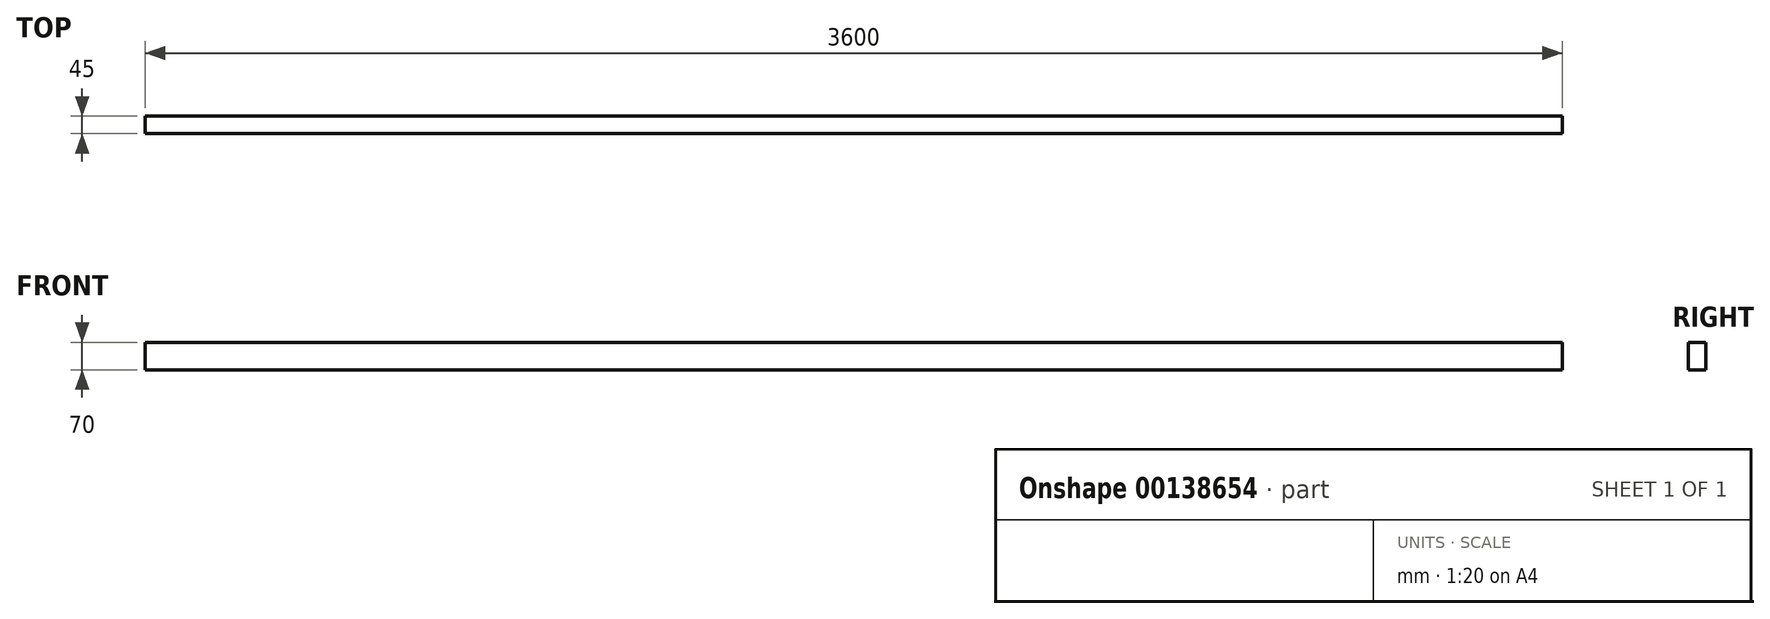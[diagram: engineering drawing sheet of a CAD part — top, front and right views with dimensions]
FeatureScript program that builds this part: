
annotation { "Feature Type Name" : "Feature", "Feature Type Description" : "" }
export const myFeature = defineFeature(function(context is Context, id is Id, definition is map)
    precondition{}
    {
        {
            var Q0;
            Q0=qCreatedBy(makeId("Right.planeOp"),FACE);
            var sketch = newSketch(context, id + "F0", { "sketchPlane" : qUnion([Q0])});
            skLineSegment(sketch, "E0.bottom", {"start": v(22.5, 35) * mm, "end": v(-22.5, 35) * mm});
            skLineSegment(sketch, "E0.top", {"start": v(22.5, -35) * mm, "end": v(-22.5, -35) * mm});
            skLineSegment(sketch, "E0.left", {"start": v(22.5, 35) * mm, "end": v(22.5, -35) * mm});
            skLineSegment(sketch, "E0.right", {"start": v(-22.5, 35) * mm, "end": v(-22.5, -35) * mm});
            skPoint(sketch, "E0.middle", {"position": v(0, 0) * mm});
            skSolve(sketch);
        }
        {
            var Q0;
            Q0=qSketchRegion(id+"F0",true);
            extrude(context, id + "F1", {"entities" : qUnion([Q0]), "endBound" : BoundingType.SYMMETRIC, "depth" : 3600 * mm});
        }
    });
